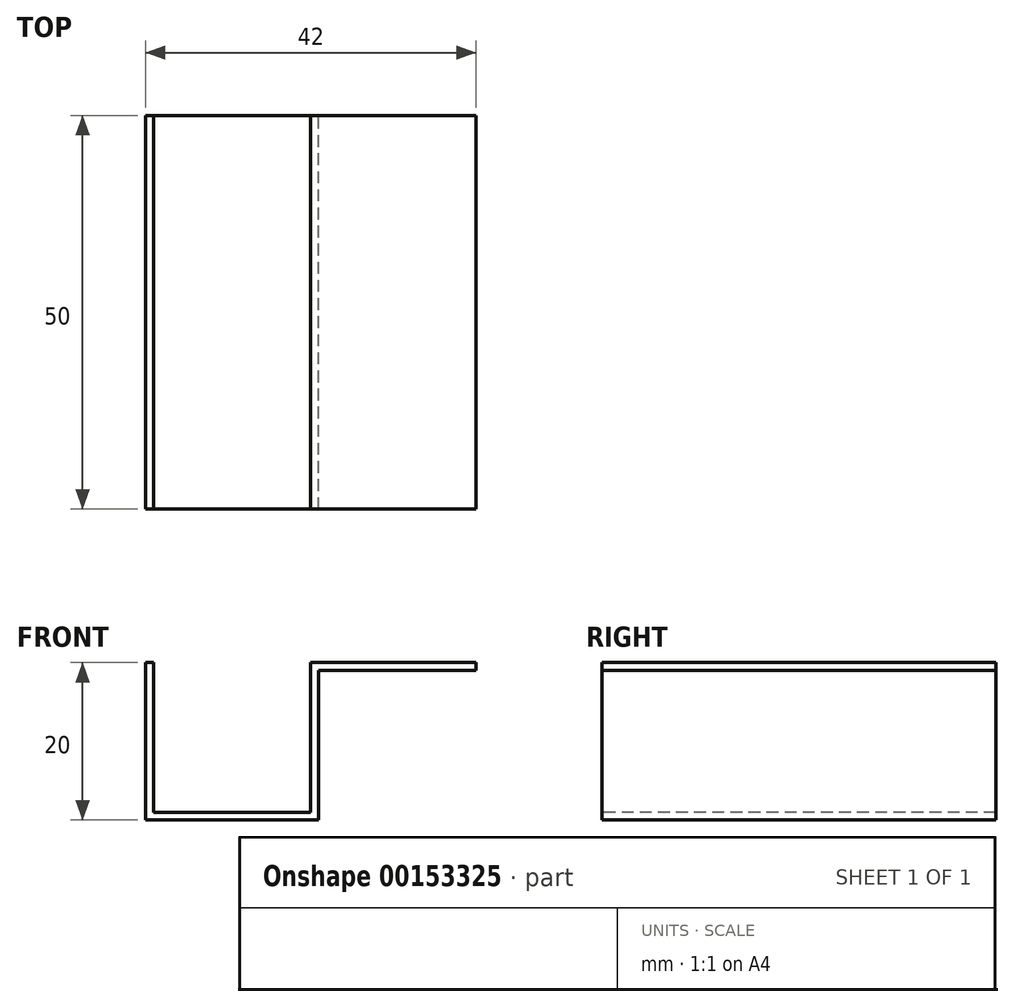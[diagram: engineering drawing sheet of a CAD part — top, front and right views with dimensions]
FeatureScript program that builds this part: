
annotation { "Feature Type Name" : "Feature", "Feature Type Description" : "" }
export const myFeature = defineFeature(function(context is Context, id is Id, definition is map)
    precondition{}
    {
        {
            var Q0;
            Q0=qCreatedBy(makeId("Top.planeOp"),FACE);
            var sketch = newSketch(context, id + "F0", { "sketchPlane" : qUnion([Q0])});
            skLineSegment(sketch, "E0.bottom", {"start": v(-77.54, 14.2) * mm, "end": v(-35.54, 14.2) * mm});
            skLineSegment(sketch, "E0.top", {"start": v(-77.54, -35.8) * mm, "end": v(-35.54, -35.8) * mm});
            skLineSegment(sketch, "E0.left", {"start": v(-77.54, 14.2) * mm, "end": v(-77.54, -35.8) * mm});
            skLineSegment(sketch, "E0.right", {"start": v(-35.54, 14.2) * mm, "end": v(-35.54, -35.8) * mm});
            skSolve(sketch);
        }
        {
            var Q0;
            Q0=makeQuery(id+"F0.imprint","IMPRINT",FACE,{"disambiguationData":[TD([[makeQuery(id+"F0.imprint","IMPRINT",EDGE,{"derivedFrom":sQuery(id+"F0.wireOp",EDGE,"E0.bottom")}),-1.0]])]});
            extrude(context, id + "F1", {"entities" : qUnion([Q0]), "depth" : 20 * mm});
        }
        {
            var Q0;
            Q0=makeQuery(id+"F1.opExtrude","CAP_FACE",FACE,{"disambiguationData":[OSD([sQuery(id+"F0.wireOp",EDGE,"E0.bottom"),sQuery(id+"F0.wireOp",EDGE,"E0.top"),sQuery(id+"F0.wireOp",EDGE,"E0.left"),sQuery(id+"F0.wireOp",EDGE,"E0.right")])],"isStart":false});
            var sketch = newSketch(context, id + "F2", { "sketchPlane" : qUnion([Q0])});
            skLineSegment(sketch, "E1", {"start": v(-76.54, 14.2) * mm, "end": v(-76.54, -35.8) * mm});
            skLineSegment(sketch, "E2", {"start": v(-56.54, 14.2) * mm, "end": v(-56.54, -35.8) * mm});
            skSolve(sketch);
        }
        {
            var Q0;
            {var subQ0=sQuery(id+"F2.wireOp",EDGE,"E1");Q0=makeQuery(id+"F2.imprint","IMPRINT",FACE,{"disambiguationData":[TD([[makeQuery(id+"F2.imprint","IMPRINT",EDGE,{"derivedFrom":subQ0}),1.0]])]});}
            extrude(context, id + "F3", {"entities" : qUnion([Q0]), "operationType" : NewBodyOperationType.REMOVE, "oppositeDirection" : true, "depth" : 19 * mm});
        }
        {
            var Q0;
            Q0=makeQuery(id+"F1.opExtrude","CAP_FACE",FACE,{"disambiguationData":[OSD([sQuery(id+"F0.wireOp",EDGE,"E0.bottom"),sQuery(id+"F0.wireOp",EDGE,"E0.top"),sQuery(id+"F0.wireOp",EDGE,"E0.left"),sQuery(id+"F0.wireOp",EDGE,"E0.right")])],"isStart":true});
            var sketch = newSketch(context, id + "F4", { "sketchPlane" : qUnion([Q0])});
            skLineSegment(sketch, "E3", {"start": v(-55.54, 35.8) * mm, "end": v(-55.54, -14.2) * mm});
            skSolve(sketch);
        }
        {
            var Q0;
            {var subQ0=sQuery(id+"F4.wireOp",EDGE,"E3");Q0=makeQuery(id+"F4.imprint","IMPRINT",FACE,{"disambiguationData":[TD([[makeQuery(id+"F4.imprint","IMPRINT",EDGE,{"derivedFrom":subQ0}),1.0]])]});}
            extrude(context, id + "F5", {"entities" : qUnion([Q0]), "operationType" : NewBodyOperationType.REMOVE, "oppositeDirection" : true, "depth" : 19 * mm});
        }
    });
